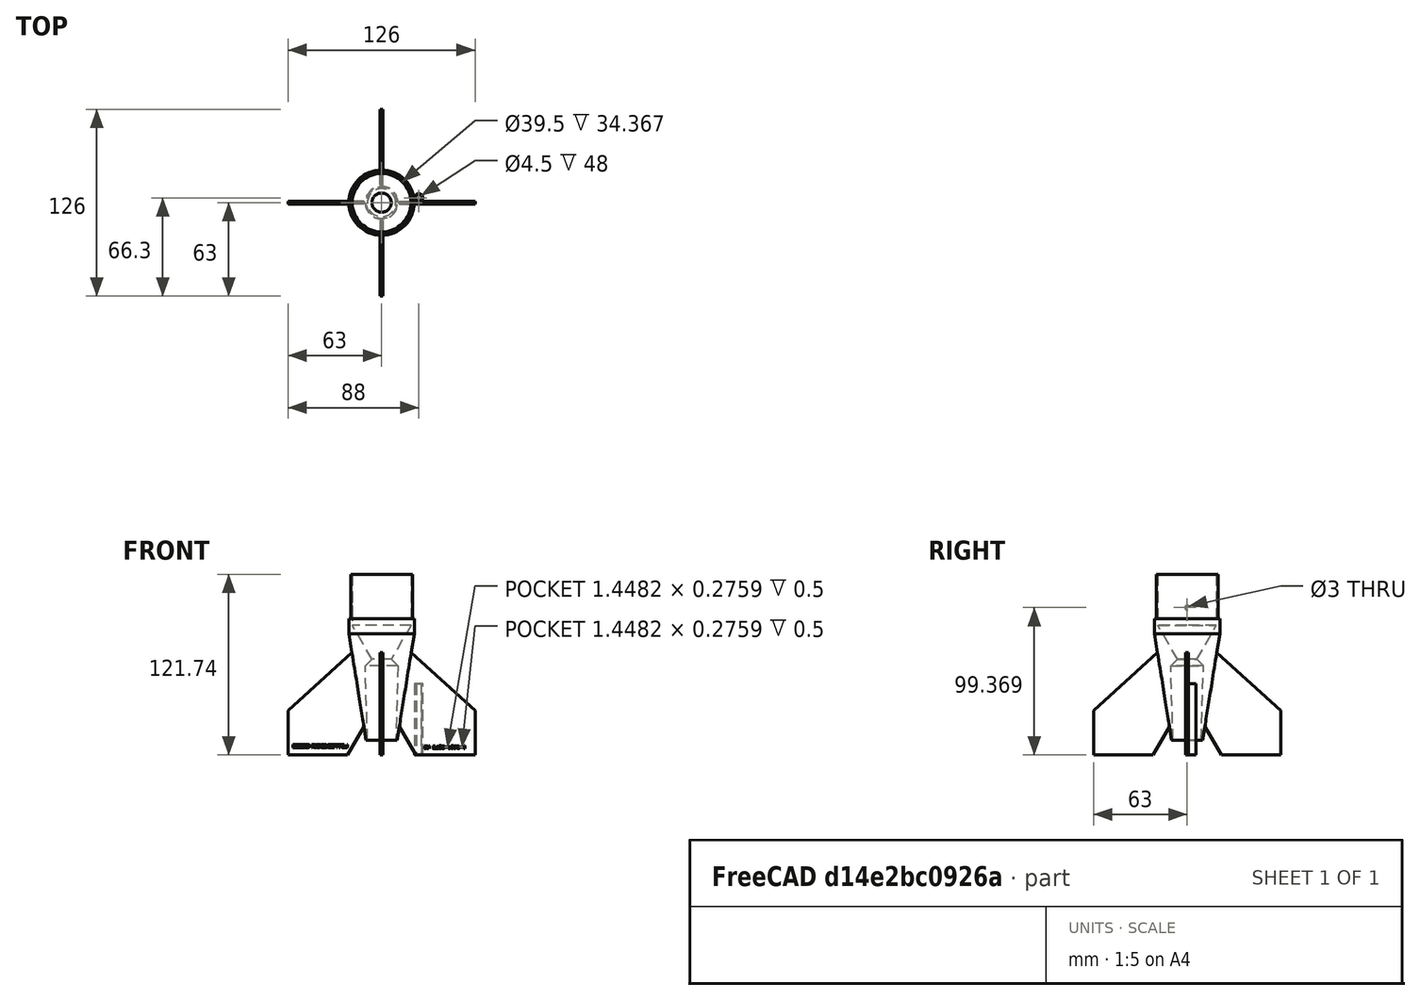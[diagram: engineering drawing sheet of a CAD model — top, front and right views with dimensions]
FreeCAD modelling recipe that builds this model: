
FCSTD DOCUMENT  (FreeCAD 0.20R29603 (Git))
Label: Ez3D-18PT
License: All rights reserved
LicenseURL: http://en.wikipedia.org/wiki/All_rights_reserved
objects: Sketcher::SketchObject×4, PartDesign::Pad×2, Part::Part2DObjectPython×2, PartDesign::Pocket×2, PartDesign::Revolution×1, PartDesign::PolarPattern×1, Mesh::Feature×1, PartDesign::Plane×1, PartDesign::Hole×1, PartDesign::Body×1
note: 21 computed .brp shape members not serialized (recipe doc carries the construction recipe); baked Part::Feature solids carry a one-line shape summary decoded from their .brp

FEATURE [Sketcher::SketchObject] Sketch  label="Motor tube"
  FullyConstrained = false
  MapMode = 5
  Placement = pos=(0,0,0) rot=(1,0,0;1.5708rad)
  Support = -> [XZ_Plane]
  sketch-geometry (10):
    g0: LineSegment StartX=9.5 StartY=10 StartZ=0 EndX=10.5 EndY=10 EndZ=0
    g1: LineSegment StartX=6.5 StartY=64.5 StartZ=0 EndX=11 EndY=60 EndZ=0
    g2: LineSegment StartX=11 StartY=60 StartZ=0 EndX=9.5 EndY=10 EndZ=0
    g3: LineSegment StartX=19.75 StartY=121.736 StartZ=0 EndX=19.75 EndY=87.3689 EndZ=0
    g4: LineSegment StartX=19.75 StartY=87.3689 StartZ=0 EndX=6.5 EndY=64.5 EndZ=0
    g5: LineSegment StartX=20.75 StartY=91.7363 StartZ=0 EndX=20.75 EndY=121.736 EndZ=0
    g6: LineSegment StartX=20.75 StartY=121.736 StartZ=0 EndX=19.75 EndY=121.736 EndZ=0
    g7: LineSegment StartX=22 StartY=81.7363 StartZ=0 EndX=10.5 EndY=10 EndZ=0
    g8: LineSegment StartX=20.75 StartY=91.7363 StartZ=0 EndX=22 EndY=91.7363 EndZ=0
    g9: LineSegment StartX=22 StartY=91.7363 StartZ=0 EndX=22 EndY=81.7363 EndZ=0
  constraints (28):
    c: Coincident(g1,g2)
    c: DistanceX(g0,g0) = 1
    c: DistanceX(g-1,g0) = 9.5
    c: Angle(g1) = -0.785398
    c: Vertical(g3)
    c: Coincident(g3,g4)
    c: Vertical(g5)
    c: Coincident(g5,g6)
    c: Coincident(g6,g3)
    c: Horizontal(g6)
    c: DistanceX(g-1,g5) = 20.75
    c: DistanceX(g6,g6) = 1
    c: Coincident(g2,g0)
    c: DistanceY(g-1,g0) = 10
    c: Horizontal(g0)
    c: Coincident(g7,g0)
    c: Horizontal(g8)
    c: Coincident(g9,g8)
    c: Vertical(g9)
    c: Coincident(g5,g8)
    c: DistanceX(g8) = 22
    c: DistanceY(g9,g9) = 10
    c: DistanceY(g5,g5) = 30
    c: DistanceY(g-1,g1) = 60
    c: DistanceX(g-1,g1) = 6.5
    c: Coincident(g9,g7)
    c: DistanceX(g-1,g1) = 11
    c: Coincident(g1,g4)
FEATURE [PartDesign::Revolution] Revolution  label="Motor Tube"
  Angle = 360
  Axis = (0,-2e-16,1)
  Base = (0,0,0)
  Placement = pos=(0,0,0) rot=(1,0,0;1.5708rad)
  Profile = -> Sketch
  ReferenceAxis = -> Sketch [V_Axis]
  Reversed = true
FEATURE [Sketcher::SketchObject] Sketch001  label="Fin Pattern"
  FullyConstrained = false
  MapMode = 5
  Placement = pos=(0,0,0) rot=(1,0,0;1.5708rad)
  Support = -> [XZ_Plane]
  sketch-geometry (5):
    g0: LineSegment StartX=23 StartY=0 StartZ=0 EndX=63 EndY=0 EndZ=0
    g1: LineSegment StartX=63 StartY=0 StartZ=0 EndX=63 EndY=30 EndZ=0
    g2: LineSegment StartX=63 StartY=30 StartZ=0 EndX=13.5454 EndY=75 EndZ=0
    g3: LineSegment StartX=13.5454 StartY=75 StartZ=0 EndX=10.851 EndY=21.0426 EndZ=0
    g4: LineSegment StartX=10.851 StartY=21.0426 StartZ=0 EndX=23 EndY=0 EndZ=0
  constraints (13):
    c: Horizontal(g0)
    c: Coincident(g0,g1)
    c: Coincident(g1,g2)
    c: Vertical(g1)
    c: Coincident(g3,g4)
    c: Coincident(g0,g4)
    c: Angle(g4) = -1.0472
    c: PointOnObject(g0,g-1)
    c: DistanceY(g1,g1) = 30
    c: DistanceX(g-1,g0) = 23
    c: DistanceY(g-1,g2) = 75
    c: DistanceX(g0,g0) = 40
    c: Coincident(g2,g3)
FEATURE [PartDesign::Pad] Pad  label="Fins"
  BaseFeature = -> Revolution
  Direction = (0,-1,-2e-16)
  Length = 2
  Length2 = 100
  Midplane = true
  Placement = pos=(0,0,0) rot=(1,0,0;1.5708rad)
  Profile = -> Sketch001
  Type = 0
FEATURE [PartDesign::PolarPattern] PolarPattern  label="PolarPattern for 4 fins"
  Angle = 360
  Axis = -> Z_Axis
  BaseFeature = -> Pad
  Occurrences = 4
  Originals = -> [Pad]
  Placement = pos=(0,0,0) rot=(1,0,0;1.5708rad)
FEATURE [Sketcher::SketchObject] Sketch002  label="Launch Lug"
  FullyConstrained = true
  MapMode = 5
  Support = -> [XY_Plane]
  sketch-geometry (2):
    g0: Circle CenterX=25 CenterY=3.3 CenterZ=0 NormalX=0 NormalY=0 NormalZ=1 AngleXU=0 Radius=2.75
    g1: Circle CenterX=25 CenterY=3.3 CenterZ=0 NormalX=0 NormalY=0 NormalZ=1 AngleXU=0 Radius=2.25
  constraints (5):
    c: Coincident(g1,g0)
    c: Diameter(g0) = 5.5
    c: Diameter(g1) = 4.5
    c: DistanceY(g-1,g0) = 3.3
    c: DistanceX(g-1,g0) = 25
FEATURE [PartDesign::Pad] Pad001  label="Launch Lug001"
  BaseFeature = -> PolarPattern
  Direction = (0,0,1)
  Length = 48
  Length2 = 100
  Placement = pos=(0,0,0) rot=(1,0,0;1.5708rad)
  Profile = -> Sketch002
  ReferenceAxis = -> Sketch002 [N_Axis]
  Type = 0
FEATURE [Mesh::Feature] Thread_24x3_9_5Rad_10mmTall_v1  label="Thread-24x3-9.5Rad-10mmTall v1"
FEATURE [PartDesign::Plane] DatumPlane
  Length = 163.867
  MapMode = 5
  Placement = pos=(1,-1e-16,-2e-16) rot=(0.707107,0,0.707107;3.14159rad)
  ResizeMode = 0
  Support = -> [Pad001]
  Width = 67.131
FEATURE [Sketcher::SketchObject] Sketch003  label="Recovery Harness Hole"
  FullyConstrained = false
  MapMode = 5
  Placement = pos=(1,-1e-16,-2e-16) rot=(0.707107,0,0.707107;3.14159rad)
  Support = -> [DatumPlane]
  sketch-geometry (1):
    g0: Circle CenterX=99.3688 CenterY=0 CenterZ=0 NormalX=0 NormalY=0 NormalZ=1 AngleXU=0 Radius=2.20124
  constraints (1):
    c: PointOnObject(g0,g-1)
FEATURE [PartDesign::Hole] Hole
  BaseFeature = -> Pad001
  CustomThreadClearance = 0
  Depth = 25
  DepthType = 0
  Diameter = 3
  DrillForDepth = false
  DrillPoint = 1
  DrillPointAngle = 118
  HoleCutCountersinkAngle = 90
  HoleCutCustomValues = false
  HoleCutDepth = 0
  HoleCutDiameter = 6.1
  HoleCutType = 0
  ModelThread = false
  Placement = pos=(0,0,0) rot=(1,0,0;1.5708rad)
  Profile = -> Sketch003
  Tapered = false
  TaperedAngle = 90
  ThreadClass = 0
  ThreadDepth = 25
  ThreadDepthType = 0
  ThreadDirection = 0
  ThreadFit = 0
  ThreadSize = 0
  ThreadType = 0
  Threaded = false
  UseCustomThreadClearance = false
FEATURE [Part::Part2DObjectPython] ShapeString  label="Logo"  # Draft 2D object (typed FeaturePython)
  FontFile = <path>
  MakeFace = true
  Placement = pos=(-60,-1,5) rot=(1,0,0;1.5708rad)
  Size = 1.2
  String = Ez3D Rocketry
  Tracking = 0
FEATURE [Part::Part2DObjectPython] ShapeString001  label="PN"  # Draft 2D object (typed FeaturePython)
  FontFile = <path>
  MakeFace = true
  Placement = pos=(28.598,-1,4.347) rot=(1,0,0;1.5708rad)
  Size = 2.5
  String = PN Ez3D-18PT-4
  Tracking = 0
FEATURE [PartDesign::Pocket] Pocket
  BaseFeature = -> Hole
  Direction = (0,1,0)
  Length = 0.5
  Length2 = 5
  Placement = pos=(0,0,0) rot=(1,0,0;1.5708rad)
  Profile = -> ShapeString
  ReferenceAxis = -> ShapeString [N_Axis]
  Type = 0
FEATURE [PartDesign::Pocket] Pocket001
  BaseFeature = -> Pocket
  Direction = (0,1,0)
  Length = 0.5
  Length2 = 5
  Placement = pos=(0,0,0) rot=(1,0,0;1.5708rad)
  Profile = -> ShapeString001
  ReferenceAxis = -> ShapeString001 [N_Axis]
  Type = 0
FEATURE [PartDesign::Body] Body
  Group = -> [Sketch,Revolution,Sketch001,Pad,PolarPattern,Sketch002,Pad001,DatumPlane,Sketch003,Hole,ShapeString,ShapeString001,Pocket,Pocket001]
  Origin = -> Origin
  Tip = -> Pocket001
note: 2 file-system paths scrubbed to <path> (originals preserved in the JSON sidecar)
